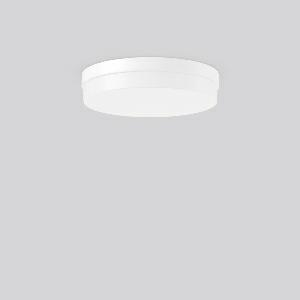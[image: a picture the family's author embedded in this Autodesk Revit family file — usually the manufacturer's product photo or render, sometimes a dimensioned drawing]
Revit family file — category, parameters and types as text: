
# Revit family: flat_kreis_221156_002_1_76_3761
name_source: partatom
category: Lighting Fixtures
units: mm (PartAtom-declared; Revit-internal decimal feet)

## family parameters
Cut with Voids When Loaded = No
Host = Face
Light Source = No
Part Type = Normal
Room Calculation Point = No
Round Connector Dimension = Use Diameter
Shared = No

## types (1)
- FLAT KREIS (1 x LED Modul 840, 1400 lm, 4000)
    Apparent Load = 19 VA
    CIE Flux Codes = 42 73 92 90 100
    Color Rendering = 80
    Color Temperature = 4000
    Default Elevation = 1800 mm
    Description = Series: FLAT KREIS
Decorative round surface-mounted luminaire. Base: plastic. Diffuser: plastic (polypropylene), opal. Diffuser fastening: spring system. Homogeneous and smooth light distribution. 
Colour: white
Diameter: 380 mm
Height: 78 mm
Lamp: LED exchangeable
Socket: without socket
Colour temperature: 4000K
Colour rendering index (CRI): 80
System power: 19 W
Rated luminous flux: 1400 lm
Beam angle Down: 121°
Luminous efficiency: 74 lm/W
Control gear: AC power, DALI dimmable
Protection class: I
Type of protection: IP 43
    Height = 78 mm
    Lamp = 1 x LED Modul 840
    Lamp Light Flux = 1400 lm
    Lamp count = 1
    Length = 380 mm
    Lifetime = 50000 h
    Luminous efficacy = 74 lm/W
    Manufacturer = RZB
    ModVariant = No
    Model = 221156.002.1.76
    Mounting Place = Ceiling, Wall
    Mounting Type = Surface mounted
    Number of Poles = 1
    OnlyDefault = Yes
    Power Factor = 1
    Product Name = FLAT KREIS
    Product group = Surface mounted ceiling and wall luminaires
    ProductGroupID = 305
    Protection Class = Protection class I
    Protection Degree = IP 43
    RLX_Detail_Level = 1
    RLX_Emergency_Light_Flux = 0 lm
    RLX_Emergency_Type = 0
    RLX_Emergency_Type_DB = No
    RlxData = <blob elided: 12877 chars, md5=dffe4749>
    Socket = socket
    Standby Power = 0 W
    System Light Flux = 1400 lm
    System Power = 19 W
    Type Comments = ALEA SPOT
    Type Image = 221062.862.79.jpg
    URL = http://relux.com
    VarID = ---
    Voltage = 230 V
    Voltage Range = 220-240 V
    Weight = 0.00 kg
    Width = 0 mm  [stored 0 ft]

note: [stored X ft] marks values corroborated as IEEE doubles in the binary element streams (Revit-internal decimal feet)

## geometry (parser evidence)
native form markers: Sweep x11
no freeform markers — native parametric forms only
